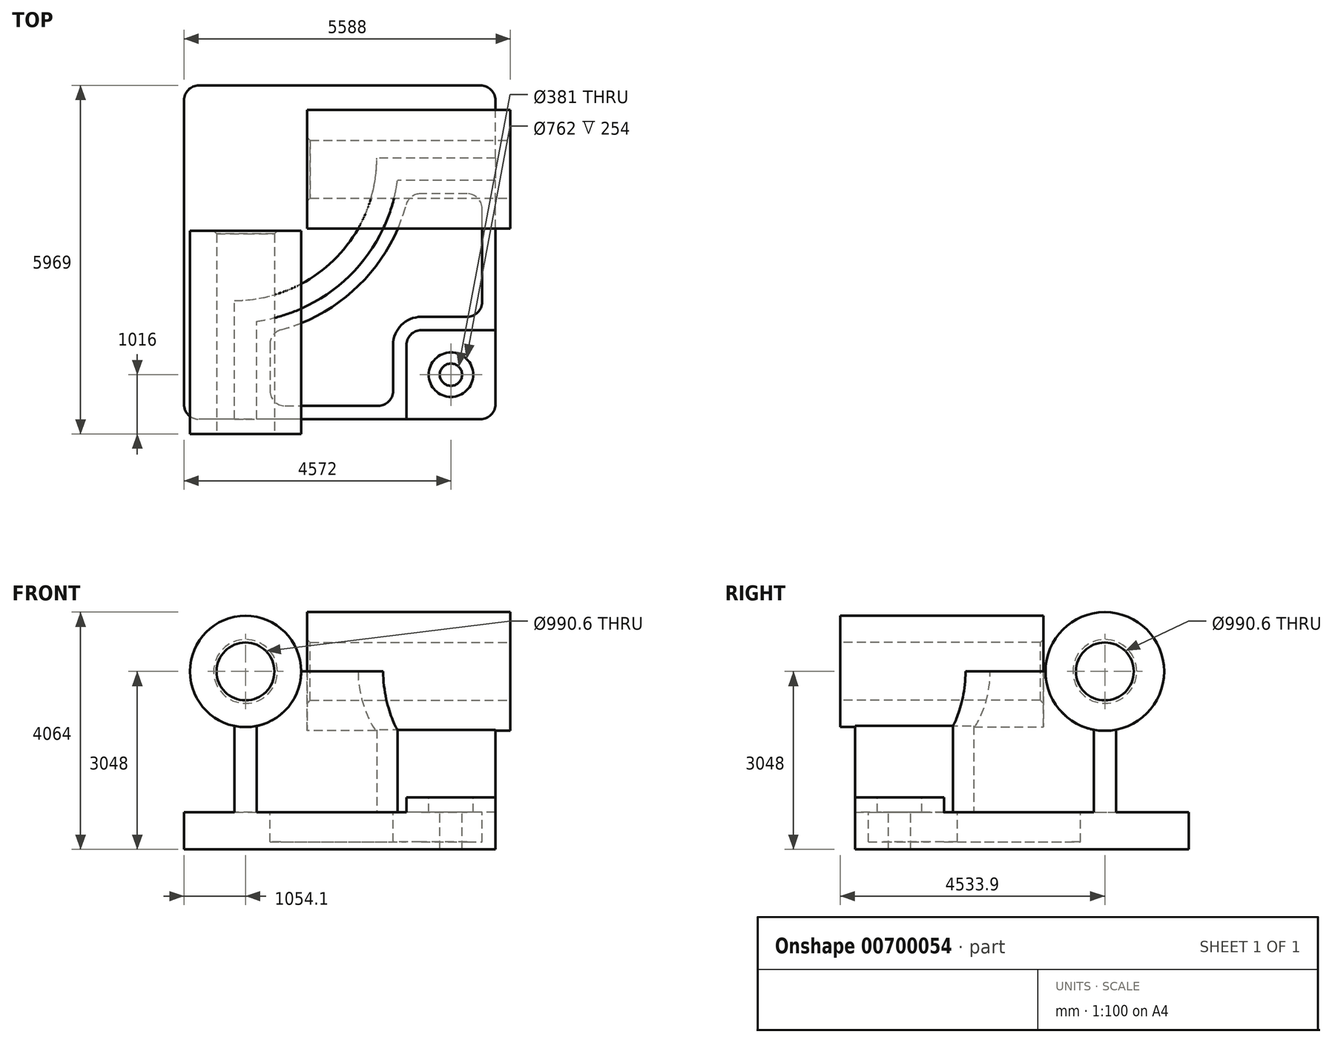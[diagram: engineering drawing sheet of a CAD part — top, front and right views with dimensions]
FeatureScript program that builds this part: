
annotation { "Feature Type Name" : "Feature", "Feature Type Description" : "" }
export const myFeature = defineFeature(function(context is Context, id is Id, definition is map)
    precondition{}
    {
        {
            var Q0;
            Q0=qCreatedBy(makeId("Top.planeOp"),FACE);
            var sketch = newSketch(context, id + "F0", { "sketchPlane" : qUnion([Q0])});
            skLineSegment(sketch, "E0.bottom", {"start": v(2736.66, -2857.5) * mm, "end": v(-2597.34, -2857.5) * mm});
            skLineSegment(sketch, "E0.top", {"start": v(2736.66, 2857.5) * mm, "end": v(-2597.34, 2857.5) * mm});
            skLineSegment(sketch, "E0.left", {"start": v(2736.66, -2857.5) * mm, "end": v(2736.66, 2857.5) * mm});
            skLineSegment(sketch, "E0.right", {"start": v(-2597.34, -2857.5) * mm, "end": v(-2597.34, 2857.5) * mm});
            skPoint(sketch, "E0.middle", {"position": v(69.66, 0) * mm});
            skSolve(sketch);
        }
        {
            var Q0;
            Q0=makeQuery(id+"F0.imprint","IMPRINT",FACE,{"disambiguationData":[TD([[makeQuery(id+"F0.imprint","IMPRINT",EDGE,{"derivedFrom":sQuery(id+"F0.wireOp",EDGE,"E0.bottom")}),-1.0]])]});
            extrude(context, id + "F1", {"entities" : qUnion([Q0]), "depth" : 635 * mm, "offsetDistance" : 25.4 * mm});
        }
        {
            var Q0;
            Q0=makeQuery(id+"F1.opExtrude","CAP_FACE",FACE,{"disambiguationData":[OSD([sQuery(id+"F0.wireOp",EDGE,"E0.bottom"),sQuery(id+"F0.wireOp",EDGE,"E0.top"),sQuery(id+"F0.wireOp",EDGE,"E0.left"),sQuery(id+"F0.wireOp",EDGE,"E0.right")])],"isStart":false});
            var sketch = newSketch(context, id + "F2", { "sketchPlane" : qUnion([Q0])});
            skLineSegment(sketch, "E1", {"start": v(-1733.74, -2857.5) * mm, "end": v(-1733.74, -825.5) * mm});
            skLineSegment(sketch, "E2", {"start": v(2736.66, 1612.9) * mm, "end": v(704.66, 1612.9) * mm});
            skArc(sketch, "E3", {"start": v(-1733.74, -825.5) * mm, "mid": v(-9.53, -111.3) * mm, "end": v(704.66, 1612.9) * mm});
            skLineSegment(sketch, "E4", {"start": v(-1733.74, 1612.9) * mm, "end": v(704.66, 1612.9) * mm, "construction": true});
            skLineSegment(sketch, "E5", {"start": v(-1733.74, -825.5) * mm, "end": v(-1733.74, 1612.9) * mm, "construction": true});
            skLineSegment(sketch, "E6.0", {"start": v(-1352.74, -2857.5) * mm, "end": v(-1352.74, -1180.64) * mm});
            skArc(sketch, "E6.1", {"start": v(-1352.74, -1180.64) * mm, "mid": v(259.88, -380.72) * mm, "end": v(1059.8, 1231.9) * mm});
            skLineSegment(sketch, "E6.2", {"start": v(2736.66, 1231.9) * mm, "end": v(1059.8, 1231.9) * mm});
            skLineSegment(sketch, "E7.0", {"start": v(2736.66, -2857.5) * mm, "end": v(2736.66, 2857.5) * mm});
            skLineSegment(sketch, "E8.0", {"start": v(2736.66, -2857.5) * mm, "end": v(-2597.34, -2857.5) * mm});
            skSolve(sketch);
        }
        {
            var Q0;
            {var subQ2=sQuery(id+"F2.wireOp",EDGE,"E1");Q0=makeQuery(id+"F2.imprint","IMPRINT",FACE,{"disambiguationData":[TD([[makeQuery(id+"F2.imprint","IMPRINT",EDGE,{"derivedFrom":subQ2}),-1.0]])]});}
            extrude(context, id + "F3", {"entities" : qUnion([Q0]), "operationType" : NewBodyOperationType.ADD, "depth" : 2413 * mm, "offsetDistance" : 25.4 * mm});
        }
        {
            var Q0;
            Q0=makeQuery(id+"F3.boolean.opBoolean","MERGE",FACE,{"derivedFrom":[makeQuery(id+"F1.opExtrude","SWEPT_FACE",FACE,{"disambiguationData":[OSD([sQuery(id+"F0.wireOp",EDGE,"E0.bottom")])]}),makeQuery(id+"F3.opExtrude","SWEPT_FACE",FACE,{"disambiguationData":[OSD([sQuery(id+"F2.wireOp",EDGE,"E8.0")])]})]});
            var sketch = newSketch(context, id + "F4", { "sketchPlane" : qUnion([Q0])});
            skCircle(sketch, "E9", {"center": v(-1543.24, 3048) * mm, "radius": 952.5 * mm});
            skSolve(sketch);
        }
        {
            var Q0;
            {var subQ1=sQuery(id+"F2.wireOp",EDGE,"E8.0");var subQ6=makeQuery(id+"F3.opExtrude","CAP_EDGE",EDGE,{"disambiguationData":[OSD([subQ1])],"isStart":false});Q0=makeQuery(id+"F4.imprint","IMPRINT",FACE,{"disambiguationData":[TD([[makeQuery(id+"F4.imprint","IMPRINT",EDGE,{"derivedFrom":subQ6}),-1.0]])]});}
            var Q1;
            {var subQ1=sQuery(id+"F2.wireOp",EDGE,"E8.0");var subQ6=makeQuery(id+"F3.opExtrude","CAP_EDGE",EDGE,{"disambiguationData":[OSD([subQ1])],"isStart":false});Q1=makeQuery(id+"F4.imprint","IMPRINT",FACE,{"disambiguationData":[TD([[makeQuery(id+"F4.imprint","IMPRINT",EDGE,{"derivedFrom":subQ6}),1.0]])]});}
            extrude(context, id + "F5", {"entities" : qUnion([Q0, Q1]), "operationType" : NewBodyOperationType.ADD, "depth" : 254 * mm, "offsetDistance" : 25.4 * mm, "hasSecondDirection" : true, "secondDirectionOppositeDirection" : true, "secondDirectionDepth" : 3225.8 * mm});
        }
        {
            var Q0;
            Q0=makeQuery(id+"F3.boolean.opBoolean","MERGE",FACE,{"derivedFrom":[makeQuery(id+"F1.opExtrude","SWEPT_FACE",FACE,{"disambiguationData":[OSD([sQuery(id+"F0.wireOp",EDGE,"E0.left")])]}),makeQuery(id+"F3.opExtrude","SWEPT_FACE",FACE,{"disambiguationData":[OSD([sQuery(id+"F2.wireOp",EDGE,"E7.0")])]})]});
            var sketch = newSketch(context, id + "F6", { "sketchPlane" : qUnion([Q0])});
            skCircle(sketch, "E10", {"center": v(1422.4, 3048) * mm, "radius": 1016 * mm});
            skSolve(sketch);
        }
        {
            var Q0;
            {var subQ1=sQuery(id+"F2.wireOp",EDGE,"E7.0");var subQ6=makeQuery(id+"F3.opExtrude","CAP_EDGE",EDGE,{"disambiguationData":[OSD([subQ1])],"isStart":false});Q0=makeQuery(id+"F6.imprint","IMPRINT",FACE,{"disambiguationData":[TD([[makeQuery(id+"F6.imprint","IMPRINT",EDGE,{"derivedFrom":subQ6}),1.0]])]});}
            var Q1;
            {var subQ1=sQuery(id+"F2.wireOp",EDGE,"E7.0");var subQ6=makeQuery(id+"F3.opExtrude","CAP_EDGE",EDGE,{"disambiguationData":[OSD([subQ1])],"isStart":false});Q1=makeQuery(id+"F6.imprint","IMPRINT",FACE,{"disambiguationData":[TD([[makeQuery(id+"F6.imprint","IMPRINT",EDGE,{"derivedFrom":subQ6}),-1.0]])]});}
            extrude(context, id + "F7", {"entities" : qUnion([Q0, Q1]), "operationType" : NewBodyOperationType.ADD, "depth" : 254 * mm, "offsetDistance" : 25.4 * mm, "hasSecondDirection" : true, "secondDirectionOppositeDirection" : true, "secondDirectionDepth" : 3225.8 * mm});
        }
        {
            var Q0;
            {var subQ0=sQuery(id+"F0.wireOp",EDGE,"E0.left");var subQ1=sQuery(id+"F0.wireOp",EDGE,"E0.bottom");Q0=makeQuery(id+"F3.boolean.opBoolean","SPLIT",FACE,{"disambiguationData":[TD([makeQuery(id+"F3.opExtrude","SWEPT_FACE",FACE,{"disambiguationData":[OSD([sQuery(id+"F2.wireOp",EDGE,"E6.0")])]})])],"derivedFrom":makeQuery(id+"F1.opExtrude","CAP_FACE",FACE,{"disambiguationData":[OSD([subQ1,sQuery(id+"F0.wireOp",EDGE,"E0.top"),subQ0,sQuery(id+"F0.wireOp",EDGE,"E0.right")])],"isStart":false})});}
            var sketch = newSketch(context, id + "F8", { "sketchPlane" : qUnion([Q0])});
            skLineSegment(sketch, "E11.bottom", {"start": v(2736.66, -2857.5) * mm, "end": v(1212.66, -2857.5) * mm});
            skLineSegment(sketch, "E11.top", {"start": v(2736.66, -1333.5) * mm, "end": v(1212.66, -1333.5) * mm});
            skLineSegment(sketch, "E11.left", {"start": v(2736.66, -2857.5) * mm, "end": v(2736.66, -1333.5) * mm});
            skLineSegment(sketch, "E11.right", {"start": v(1212.66, -2857.5) * mm, "end": v(1212.66, -1333.5) * mm});
            skSolve(sketch);
        }
        {
            var Q0;
            Q0 = qSketchRegion(id + "F8", true);
            extrude(context, id + "F9", {"entities" : qUnion([Q0]), "operationType" : NewBodyOperationType.ADD, "depth" : 254 * mm, "offsetDistance" : 25.4 * mm});
        }
        {
            var Q0;
            Q0=makeQuery(id+"F9.opExtrude","SWEPT_EDGE",EDGE,{"disambiguationData":[OSD([sQuery(id+"F8.wireOp",EDGE,"E11.top"),sQuery(id+"F8.wireOp",EDGE,"E11.right")])]});
            fillet(context, id + "F10", {"entities" : qUnion([Q0]), "radius" : 254 * mm, "tangentPropagation" : true, "allowEdgeOverflow" : false});
        }
        {
            var Q0;
            {var subQ0=sQuery(id+"F0.wireOp",EDGE,"E0.left");var subQ1=sQuery(id+"F0.wireOp",EDGE,"E0.bottom");Q0=makeQuery(id+"F3.boolean.opBoolean","SPLIT",FACE,{"disambiguationData":[TD([makeQuery(id+"F3.opExtrude","SWEPT_FACE",FACE,{"disambiguationData":[OSD([sQuery(id+"F2.wireOp",EDGE,"E6.0")])]})])],"derivedFrom":makeQuery(id+"F1.opExtrude","CAP_FACE",FACE,{"disambiguationData":[OSD([subQ1,sQuery(id+"F0.wireOp",EDGE,"E0.top"),subQ0,sQuery(id+"F0.wireOp",EDGE,"E0.right")])],"isStart":false})});}
            var sketch = newSketch(context, id + "F11", { "sketchPlane" : qUnion([Q0])});
            skLineSegment(sketch, "E12.0", {"start": v(-1124.14, -1373.52) * mm, "end": v(-1124.14, -2628.9) * mm});
            skArc(sketch, "E12.1", {"start": v(1252.68, 1003.3) * mm, "mid": v(421.52, -542.36) * mm, "end": v(-1124.14, -1373.52) * mm});
            skLineSegment(sketch, "E12.2", {"start": v(-1124.14, -2628.9) * mm, "end": v(984.06, -2628.9) * mm});
            skLineSegment(sketch, "E12.3", {"start": v(2508.06, 1003.3) * mm, "end": v(1252.68, 1003.3) * mm});
            skLineSegment(sketch, "E12.4", {"start": v(984.06, -2628.9) * mm, "end": v(984.06, -1587.5) * mm});
            skArc(sketch, "E12.5", {"start": v(984.06, -1587.5) * mm, "mid": v(1125.41, -1246.25) * mm, "end": v(1466.66, -1104.9) * mm});
            skLineSegment(sketch, "E12.6", {"start": v(1466.66, -1104.9) * mm, "end": v(2508.06, -1104.9) * mm});
            skLineSegment(sketch, "E12.7", {"start": v(2508.06, -1104.9) * mm, "end": v(2508.06, 1003.3) * mm});
            skSolve(sketch);
        }
        {
            var Q0;
            Q0=makeQuery(id+"F11.imprint","IMPRINT",FACE,{"disambiguationData":[TD([[makeQuery(id+"F11.imprint","IMPRINT",EDGE,{"derivedFrom":sQuery(id+"F11.wireOp",EDGE,"E12.0")}),1.0]])]});
            extrude(context, id + "F12", {"entities" : qUnion([Q0]), "operationType" : NewBodyOperationType.REMOVE, "oppositeDirection" : true, "depth" : 508 * mm, "offsetDistance" : 25.4 * mm});
        }
        {
            var Q0;
            Q0=makeQuery(id+"F9.opExtrude","CAP_FACE",FACE,{"disambiguationData":[OSD([sQuery(id+"F8.wireOp",EDGE,"E11.bottom"),sQuery(id+"F8.wireOp",EDGE,"E11.top"),sQuery(id+"F8.wireOp",EDGE,"E11.left"),sQuery(id+"F8.wireOp",EDGE,"E11.right")])],"isStart":false});
            var sketch = newSketch(context, id + "F13", { "sketchPlane" : qUnion([Q0])});
            skCircle(sketch, "E13", {"center": v(1974.66, -2095.5) * mm, "radius": 381 * mm});
            skPoint(sketch, "E13.centerSnap0", {"position": v(1974.66, -2857.5) * mm});
            skSolve(sketch);
        }
        {
            var Q0;
            Q0=sQuery(id+"F13.wireOp",VERTEX,"E13.center");
            var Q1;
            Q1=makeQuery(id+"F1.opExtrude","SWEPT_BODY",BODY,{"disambiguationData":[OSD([sQuery(id+"F0.wireOp",EDGE,"E0.bottom"),sQuery(id+"F0.wireOp",EDGE,"E0.top"),sQuery(id+"F0.wireOp",EDGE,"E0.left"),sQuery(id+"F0.wireOp",EDGE,"E0.right")])]});
            hole(context, id + "F14", {"style" : HoleStyle.C_BORE, "endStyle" : HoleEndStyle.THROUGH, "holeDiameter" : 381 * mm, "cBoreDiameter" : 762 * mm, "cBoreDepth" : 254 * mm, "majorDiameter" : 6.35 * mm, "isTappedThrough" : true, "tappedDepth" : 12.7 * mm, "tapClearance" : 3, "locations" : qUnion([Q0]), "scope" : qUnion([Q1])});
        }
        {
            var Q0;
            Q0=makeQuery(id+"F12.boolean.opBoolean","COPY",EDGE,{"derivedFrom":makeQuery(id+"F12.opExtrude","SWEPT_EDGE",EDGE,{"disambiguationData":[OSD([sQuery(id+"F11.wireOp",EDGE,"E12.1"),sQuery(id+"F11.wireOp",EDGE,"E12.3")])]})});
            var Q1;
            Q1=makeQuery(id+"F12.boolean.opBoolean","COPY",EDGE,{"derivedFrom":makeQuery(id+"F12.opExtrude","SWEPT_EDGE",EDGE,{"disambiguationData":[OSD([sQuery(id+"F11.wireOp",EDGE,"E12.3"),sQuery(id+"F11.wireOp",EDGE,"E12.7")])]})});
            var Q2;
            Q2=makeQuery(id+"F12.boolean.opBoolean","COPY",EDGE,{"derivedFrom":makeQuery(id+"F12.opExtrude","SWEPT_EDGE",EDGE,{"disambiguationData":[OSD([sQuery(id+"F11.wireOp",EDGE,"E12.6"),sQuery(id+"F11.wireOp",EDGE,"E12.7")])]})});
            var Q3;
            Q3=makeQuery(id+"F12.boolean.opBoolean","COPY",EDGE,{"derivedFrom":makeQuery(id+"F12.opExtrude","SWEPT_EDGE",EDGE,{"disambiguationData":[OSD([sQuery(id+"F11.wireOp",EDGE,"E12.0"),sQuery(id+"F11.wireOp",EDGE,"E12.1")])]})});
            var Q4;
            Q4=makeQuery(id+"F12.boolean.opBoolean","COPY",EDGE,{"derivedFrom":makeQuery(id+"F12.opExtrude","SWEPT_EDGE",EDGE,{"disambiguationData":[OSD([sQuery(id+"F11.wireOp",EDGE,"E12.0"),sQuery(id+"F11.wireOp",EDGE,"E12.2")])]})});
            var Q5;
            Q5=makeQuery(id+"F12.boolean.opBoolean","COPY",EDGE,{"derivedFrom":makeQuery(id+"F12.opExtrude","SWEPT_EDGE",EDGE,{"disambiguationData":[OSD([sQuery(id+"F11.wireOp",EDGE,"E12.2"),sQuery(id+"F11.wireOp",EDGE,"E12.4")])]})});
            fillet(context, id + "F15", {"entities" : qUnion([Q0, Q1, Q2, Q3, Q4, Q5]), "radius" : 254 * mm, "tangentPropagation" : true, "allowEdgeOverflow" : false});
        }
        {
            var Q0;
            Q0=makeQuery(id+"F5.opExtrude","CAP_FACE",FACE,{"disambiguationData":[OSD([sQuery(id+"F4.wireOp",EDGE,"E9")])],"isStart":false});
            var sketch = newSketch(context, id + "F16", { "sketchPlane" : qUnion([Q0])});
            skCircle(sketch, "E14", {"center": v(-1543.24, 3048) * mm, "radius": 495.3 * mm});
            skSolve(sketch);
        }
        {
            var Q0;
            Q0=makeQuery(id+"F16.imprint","IMPRINT",FACE,{"disambiguationData":[TD([[makeQuery(id+"F16.imprint","IMPRINT",EDGE,{"derivedFrom":sQuery(id+"F16.wireOp",EDGE,"E14")}),1.0]])]});
            extrude(context, id + "F17", {"entities" : qUnion([Q0]), "operationType" : NewBodyOperationType.REMOVE, "oppositeDirection" : true, "depth" : 4470.4 * mm, "offsetDistance" : 25.4 * mm});
        }
        {
            var Q0;
            Q0=makeQuery(id+"F7.opExtrude","CAP_FACE",FACE,{"disambiguationData":[OSD([sQuery(id+"F6.wireOp",EDGE,"E10")])],"isStart":false});
            var sketch = newSketch(context, id + "F18", { "sketchPlane" : qUnion([Q0])});
            skCircle(sketch, "E15", {"center": v(1422.4, 3048) * mm, "radius": 495.3 * mm});
            skSolve(sketch);
        }
        {
            var Q0;
            Q0 = qSketchRegion(id + "F18", true);
            extrude(context, id + "F19", {"entities" : qUnion([Q0]), "operationType" : NewBodyOperationType.REMOVE, "oppositeDirection" : true, "depth" : 3835.4 * mm, "offsetDistance" : 25.4 * mm});
        }
        {
            var Q0;
            Q0=makeQuery(id+"F17.boolean.opBoolean","COPY",EDGE,{"derivedFrom":makeQuery(id+"F17.opExtrude","CAP_EDGE",EDGE,{"disambiguationData":[OSD([sQuery(id+"F16.wireOp",EDGE,"E14")])],"isStart":true})});
            var Q1;
            Q1=makeQuery(id+"F19.boolean.opBoolean","COPY",EDGE,{"derivedFrom":makeQuery(id+"F19.opExtrude","CAP_EDGE",EDGE,{"disambiguationData":[OSD([sQuery(id+"F18.wireOp",EDGE,"E15")])],"isStart":true})});
            var Q2;
            Q2=makeQuery(id+"F17.boolean.opBoolean","INTERSECT",EDGE,{"derivedFrom":[makeQuery(id+"F5.opExtrude","CAP_FACE",FACE,{"disambiguationData":[OSD([sQuery(id+"F4.wireOp",EDGE,"E9")])],"isStart":true}),makeQuery(id+"F17.opExtrude","SWEPT_FACE",FACE,{"disambiguationData":[OSD([sQuery(id+"F16.wireOp",EDGE,"E14")])]})]});
            var Q3;
            Q3=makeQuery(id+"F19.boolean.opBoolean","INTERSECT",EDGE,{"derivedFrom":[makeQuery(id+"F7.opExtrude","CAP_FACE",FACE,{"disambiguationData":[OSD([sQuery(id+"F6.wireOp",EDGE,"E10")])],"isStart":true}),makeQuery(id+"F19.opExtrude","SWEPT_FACE",FACE,{"disambiguationData":[OSD([sQuery(id+"F18.wireOp",EDGE,"E15")])]})]});
            chamfer(context, id + "F20", {"entities" : qUnion([Q0, Q1, Q2, Q3]), "width" : 50.8 * mm, "tangentPropagation" : true});
        }
        {
            var Q0;
            Q0=makeQuery(id+"F9.boolean.opBoolean","MERGE",EDGE,{"derivedFrom":[makeQuery(id+"F1.opExtrude","SWEPT_EDGE",EDGE,{"disambiguationData":[OSD([sQuery(id+"F0.wireOp",EDGE,"E0.bottom"),sQuery(id+"F0.wireOp",EDGE,"E0.left")])]}),makeQuery(id+"F9.opExtrude","SWEPT_EDGE",EDGE,{"disambiguationData":[OSD([sQuery(id+"F8.wireOp",EDGE,"E11.bottom"),sQuery(id+"F8.wireOp",EDGE,"E11.left")])]})]});
            var Q1;
            Q1=makeQuery(id+"F1.opExtrude","SWEPT_EDGE",EDGE,{"disambiguationData":[OSD([sQuery(id+"F0.wireOp",EDGE,"E0.top"),sQuery(id+"F0.wireOp",EDGE,"E0.left")])]});
            var Q2;
            Q2=makeQuery(id+"F1.opExtrude","SWEPT_EDGE",EDGE,{"disambiguationData":[OSD([sQuery(id+"F0.wireOp",EDGE,"E0.bottom"),sQuery(id+"F0.wireOp",EDGE,"E0.right")])]});
            var Q3;
            Q3=makeQuery(id+"F1.opExtrude","SWEPT_EDGE",EDGE,{"disambiguationData":[OSD([sQuery(id+"F0.wireOp",EDGE,"E0.top"),sQuery(id+"F0.wireOp",EDGE,"E0.right")])]});
            fillet(context, id + "F21", {"entities" : qUnion([Q0, Q1, Q2, Q3]), "radius" : 254 * mm, "tangentPropagation" : true, "allowEdgeOverflow" : false});
        }
    });
